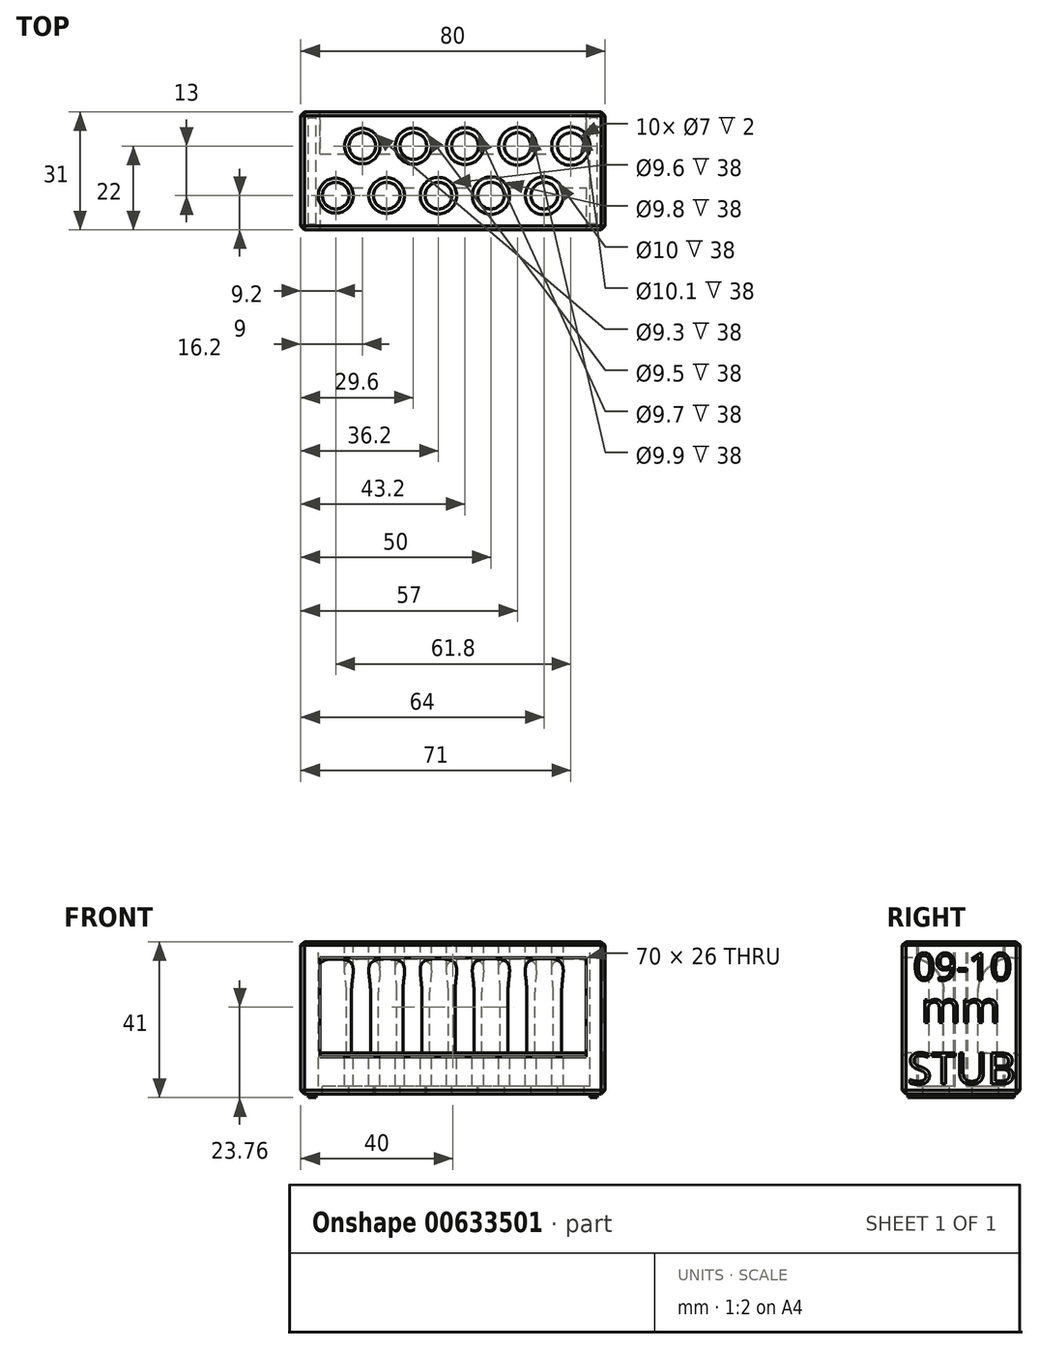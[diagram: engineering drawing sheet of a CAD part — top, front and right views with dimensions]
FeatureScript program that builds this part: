
annotation { "Feature Type Name" : "Feature", "Feature Type Description" : "" }
export const myFeature = defineFeature(function(context is Context, id is Id, definition is map)
    precondition{}
    {
        {
            var Q0;
            Q0=qCreatedBy(makeId("Top.planeOp"),FACE);
            var sketch = newSketch(context, id + "F0", { "sketchPlane" : qUnion([Q0])});
            skCircle(sketch, "E0", {"center": v(0, 0) * mm, "radius": 5.05 * mm});
            skCircle(sketch, "E1.1.0.0", {"center": v(-14, 0) * mm, "radius": 4.95 * mm});
            skCircle(sketch, "E1.2.0.0", {"center": v(-27.8, 0) * mm, "radius": 4.85 * mm});
            skCircle(sketch, "E1.3.0.0", {"center": v(-41.4, 0) * mm, "radius": 4.75 * mm});
            skCircle(sketch, "E1.4.0.0", {"center": v(-54.8, 0) * mm, "radius": 4.65 * mm});
            skLineSegment(sketch, "E1.direction1", {"start": v(0, 0) * mm, "end": v(-14, 0) * mm, "construction": true});
            skLineSegment(sketch, "E2", {"start": v(0, 0) * mm, "end": v(0, -13) * mm, "construction": true});
            skLineSegment(sketch, "E3", {"start": v(0, -13) * mm, "end": v(-90, -13) * mm, "construction": true});
            skCircle(sketch, "E4", {"center": v(-7, -13) * mm, "radius": 5 * mm});
            skCircle(sketch, "E5.1.0.0", {"center": v(-21, -13) * mm, "radius": 4.9 * mm});
            skCircle(sketch, "E5.2.0.0", {"center": v(-34.8, -13) * mm, "radius": 4.8 * mm});
            skCircle(sketch, "E5.3.0.0", {"center": v(-48.4, -13) * mm, "radius": 4.7 * mm});
            skCircle(sketch, "E5.4.0.0", {"center": v(-61.8, -13) * mm, "radius": 4.6 * mm});
            skLineSegment(sketch, "E5.direction1", {"start": v(-7, -13) * mm, "end": v(-21, -13) * mm, "construction": true});
            skSolve(sketch);
        }
        {
            var Q0;
            Q0=qCreatedBy(makeId("Top.planeOp"),FACE);
            var sketch = newSketch(context, id + "F1", { "sketchPlane" : qUnion([Q0])});
            skLineSegment(sketch, "E6.bottom", {"start": v(9, 9) * mm, "end": v(-71, 9) * mm});
            skLineSegment(sketch, "E6.top", {"start": v(9, -22) * mm, "end": v(-71, -22) * mm});
            skLineSegment(sketch, "E6.left", {"start": v(9, 9) * mm, "end": v(9, -22) * mm});
            skLineSegment(sketch, "E6.right", {"start": v(-71, 9) * mm, "end": v(-71, -22) * mm});
            skSolve(sketch);
        }
        {
            var Q0;
            Q0=makeQuery(id+"F1.imprint","IMPRINT",FACE,{"disambiguationData":[TD([[makeQuery(id+"F1.imprint","IMPRINT",EDGE,{"derivedFrom":sQuery(id+"F1.wireOp",EDGE,"E6.bottom")}),1.0]])]});
            extrude(context, id + "F2", {"entities" : qUnion([Q0]), "oppositeDirection" : true, "depth" : 40 * mm, "offsetDistance" : 25 * mm});
        }
        {
            var Q0;
            Q0=qSketchRegion(id+"F0",true);
            extrude(context, id + "F3", {"entities" : qUnion([Q0]), "operationType" : NewBodyOperationType.REMOVE, "oppositeDirection" : true, "depth" : 38 * mm, "offsetDistance" : 25 * mm});
        }
        {
            var Q0;
            Q0=qCreatedBy(makeId("Top.planeOp"),FACE);
            var sketch = newSketch(context, id + "F4", { "sketchPlane" : qUnion([Q0])});
            skLineSegment(sketch, "E7.direction1", {"start": v(0, 0) * mm, "end": v(-14, 0) * mm, "construction": true});
            skLineSegment(sketch, "E8", {"start": v(0, 0) * mm, "end": v(0, -13) * mm, "construction": true});
            skLineSegment(sketch, "E9", {"start": v(0, -13) * mm, "end": v(-90, -13) * mm, "construction": true});
            skLineSegment(sketch, "E10.direction1", {"start": v(-7, -13) * mm, "end": v(-21, -13) * mm, "construction": true});
            skCircle(sketch, "E11", {"center": v(-54.8, 0) * mm, "radius": 3.5 * mm});
            skCircle(sketch, "E12", {"center": v(-41.4, 0) * mm, "radius": 3.5 * mm});
            skCircle(sketch, "E13", {"center": v(-27.8, 0) * mm, "radius": 3.5 * mm});
            skCircle(sketch, "E14", {"center": v(-14, 0) * mm, "radius": 3.5 * mm});
            skCircle(sketch, "E15", {"center": v(0, 0) * mm, "radius": 3.5 * mm});
            skCircle(sketch, "E16", {"center": v(-61.8, -13) * mm, "radius": 3.5 * mm});
            skCircle(sketch, "E17", {"center": v(-48.4, -13) * mm, "radius": 3.5 * mm});
            skCircle(sketch, "E18", {"center": v(-34.8, -13) * mm, "radius": 3.5 * mm});
            skCircle(sketch, "E19", {"center": v(-21, -13) * mm, "radius": 3.5 * mm});
            skCircle(sketch, "E20", {"center": v(-7, -13) * mm, "radius": 3.5 * mm});
            skSolve(sketch);
        }
        {
            var Q0;
            Q0=qSketchRegion(id+"F4",true);
            extrude(context, id + "F5", {"entities" : qUnion([Q0]), "operationType" : NewBodyOperationType.REMOVE, "oppositeDirection" : true, "depth" : 50 * mm, "offsetDistance" : 25 * mm});
        }
        {
            var Q0;
            Q0=qCreatedBy(makeId("Right.planeOp"),FACE);
            var sketch = newSketch(context, id + "F6", { "sketchPlane" : qUnion([Q0])});
            skLineSegment(sketch, "E21.bottom", {"start": v(7, -4.24) * mm, "end": v(18, -4.24) * mm});
            skLineSegment(sketch, "E21.top", {"start": v(-2, -29.24) * mm, "end": v(18, -29.24) * mm});
            skLineSegment(sketch, "E21.left", {"start": v(-2, -13.24) * mm, "end": v(-2, -29.24) * mm});
            skLineSegment(sketch, "E21.right", {"start": v(18, -4.24) * mm, "end": v(18, -29.24) * mm});
            skLineSegment(sketch, "E22", {"start": v(0, 0) * mm, "end": v(-6.5, 0) * mm, "construction": true});
            skLineSegment(sketch, "E23", {"start": v(-6.5, 0) * mm, "end": v(-6.5, 18.33) * mm, "construction": true});
            skLineSegment(sketch, "E24.MirrorCS", {"start": v(-11, -13.24) * mm, "end": v(-11, -29.24) * mm});
            skLineSegment(sketch, "E25.MirrorCS", {"start": v(-31, -4.24) * mm, "end": v(-31, -29.24) * mm});
            skLineSegment(sketch, "E26.MirrorCS", {"start": v(-20, -4.24) * mm, "end": v(-31, -4.24) * mm});
            skLineSegment(sketch, "E27.MirrorCS", {"start": v(-11, -29.24) * mm, "end": v(-31, -29.24) * mm});
            skPoint(sketch, "E28.visualSharp", {"position": v(-2, -4.24) * mm});
            skArc(sketch, "E28.filletArc", {"start": v(7, -4.24) * mm, "mid": v(0.64, -6.88) * mm, "end": v(-2, -13.24) * mm});
            skPoint(sketch, "E29.visualSharp", {"position": v(-11, -4.24) * mm});
            skArc(sketch, "E29.filletArc", {"start": v(-11, -13.24) * mm, "mid": v(-13.64, -6.88) * mm, "end": v(-20, -4.24) * mm});
            skSolve(sketch);
        }
        {
            var Q0;
            Q0=qSketchRegion(id+"F6",true);
            extrude(context, id + "F7", {"entities" : qUnion([Q0]), "operationType" : NewBodyOperationType.REMOVE, "oppositeDirection" : true, "depth" : 66 * mm, "offsetDistance" : 25 * mm, "hasSecondDirection" : true, "secondDirectionOppositeDirection" : false, "secondDirectionDepth" : 4 * mm});
        }
        {
            var Q0;
            Q0=makeQuery(id+"F2.opExtrude","CAP_EDGE",EDGE,{"disambiguationData":[OSD([sQuery(id+"F1.wireOp",EDGE,"E6.right")])],"isStart":true});
            var Q1;
            Q1=makeQuery(id+"F2.opExtrude","CAP_EDGE",EDGE,{"disambiguationData":[OSD([sQuery(id+"F1.wireOp",EDGE,"E6.bottom")])],"isStart":true});
            var Q2;
            Q2=makeQuery(id+"F2.opExtrude","CAP_EDGE",EDGE,{"disambiguationData":[OSD([sQuery(id+"F1.wireOp",EDGE,"E6.top")])],"isStart":true});
            var Q3;
            Q3=makeQuery(id+"F2.opExtrude","CAP_EDGE",EDGE,{"disambiguationData":[OSD([sQuery(id+"F1.wireOp",EDGE,"E6.left")])],"isStart":true});
            var Q4;
            Q4=makeQuery(id+"F2.opExtrude","SWEPT_EDGE",EDGE,{"disambiguationData":[OSD([sQuery(id+"F1.wireOp",EDGE,"E6.top"),sQuery(id+"F1.wireOp",EDGE,"E6.right")])]});
            var Q5;
            Q5=makeQuery(id+"F2.opExtrude","CAP_EDGE",EDGE,{"disambiguationData":[OSD([sQuery(id+"F1.wireOp",EDGE,"E6.right")])],"isStart":false});
            var Q6;
            Q6=makeQuery(id+"F2.opExtrude","SWEPT_EDGE",EDGE,{"disambiguationData":[OSD([sQuery(id+"F1.wireOp",EDGE,"E6.bottom"),sQuery(id+"F1.wireOp",EDGE,"E6.right")])]});
            var Q7;
            Q7=makeQuery(id+"F2.opExtrude","SWEPT_FACE",FACE,{"disambiguationData":[OSD([sQuery(id+"F1.wireOp",EDGE,"E6.left")])]});
            var Q8;
            Q8=makeQuery(id+"F2.opExtrude","CAP_EDGE",EDGE,{"disambiguationData":[OSD([sQuery(id+"F1.wireOp",EDGE,"E6.top")])],"isStart":false});
            var Q9;
            Q9=makeQuery(id+"F2.opExtrude","CAP_EDGE",EDGE,{"disambiguationData":[OSD([sQuery(id+"F1.wireOp",EDGE,"E6.bottom")])],"isStart":false});
            var Q10;
            Q10=makeQuery(id+"F7.boolean.opBoolean","INTERSECT",EDGE,{"derivedFrom":[makeQuery(id+"F2.opExtrude","SWEPT_FACE",FACE,{"disambiguationData":[OSD([sQuery(id+"F1.wireOp",EDGE,"E6.bottom")])]}),makeQuery(id+"F7.opExtrude","SWEPT_FACE",FACE,{"disambiguationData":[OSD([sQuery(id+"F6.wireOp",EDGE,"E21.top")])]})]});
            var Q11;
            Q11=makeQuery(id+"F7.boolean.opBoolean","INTERSECT",EDGE,{"derivedFrom":[makeQuery(id+"F2.opExtrude","SWEPT_FACE",FACE,{"disambiguationData":[OSD([sQuery(id+"F1.wireOp",EDGE,"E6.top")])]}),makeQuery(id+"F7.opExtrude","SWEPT_FACE",FACE,{"disambiguationData":[OSD([sQuery(id+"F6.wireOp",EDGE,"E27.MirrorCS")])]})]});
            chamfer(context, id + "F8", {"entities" : qUnion([Q0, Q1, Q2, Q3, Q4, Q5, Q6, Q7, Q8, Q9, Q10, Q11]), "width" : 1 * mm, "tangentPropagation" : true});
        }
        {
            var Q0;
            Q0=qCreatedBy(makeId("Right.planeOp"),FACE);
            var sketch = newSketch(context, id + "F9", { "sketchPlane" : qUnion([Q0])});
            skText(sketch, "E30", { "text": "09-10", "fontName": "NotoSans-Regular.ttf"});
            skText(sketch, "E31", { "text": "mm", "fontName": "OpenSans-Regular.ttf"});
            skText(sketch, "E32", { "text": "STUB", "fontName": "OpenSans-Regular.ttf"});
            const initialGuessF9  = {"E30": [-0.019, -0.01013, 1, 0, 0.00713], "E31": [-0.017, -0.0213, 1, 0, 0.00806], "E32": [-0.0205, -0.03743, 1, 0, 0.00824]};
            skSetInitialGuess(sketch, initialGuessF9);
            skSolve(sketch);
        }
        {
            var Q0;
            Q0=qSketchRegion(id+"F9",true);
            extrude(context, id + "F10", {"entities" : qUnion([Q0]), "operationType" : NewBodyOperationType.REMOVE, "depth" : 25 * mm, "offsetDistance" : 25 * mm, "hasSecondDirection" : true, "secondDirectionOppositeDirection" : false, "secondDirectionDepth" : 8.5 * mm});
        }
        {
            var Q0;
            Q0=qCreatedBy(makeId("Top.planeOp"),FACE);
            var sketch = newSketch(context, id + "F11", { "sketchPlane" : qUnion([Q0])});
            skLineSegment(sketch, "E33.bottom", {"start": v(7, -20.5) * mm, "end": v(5, -20.5) * mm});
            skLineSegment(sketch, "E33.top", {"start": v(7, 7.5) * mm, "end": v(5, 7.5) * mm});
            skLineSegment(sketch, "E33.left", {"start": v(7, -20.5) * mm, "end": v(7, 7.5) * mm});
            skLineSegment(sketch, "E33.right", {"start": v(5, -20.5) * mm, "end": v(5, 7.5) * mm});
            skLineSegment(sketch, "E34", {"start": v(0, 0) * mm, "end": v(-31, 0) * mm, "construction": true});
            skLineSegment(sketch, "E35", {"start": v(-31, 0) * mm, "end": v(-31, -86.92) * mm, "construction": true});
            skLineSegment(sketch, "E36.MirrorCS", {"start": v(-67, -20.5) * mm, "end": v(-67, 7.5) * mm});
            skLineSegment(sketch, "E37.MirrorCS", {"start": v(-69, -20.5) * mm, "end": v(-69, 7.5) * mm});
            skLineSegment(sketch, "E38.MirrorCS", {"start": v(-69, 7.5) * mm, "end": v(-67, 7.5) * mm});
            skLineSegment(sketch, "E39.MirrorCS", {"start": v(-69, -20.5) * mm, "end": v(-67, -20.5) * mm});
            skSolve(sketch);
        }
        {
            var Q0;
            Q0=qSketchRegion(id+"F11",true);
            extrude(context, id + "F12", {"entities" : qUnion([Q0]), "operationType" : NewBodyOperationType.ADD, "oppositeDirection" : true, "depth" : 41 * mm, "offsetDistance" : 25 * mm, "hasSecondDirection" : true, "secondDirectionOppositeDirection" : true, "secondDirectionDepth" : 39 * mm});
        }
    });
